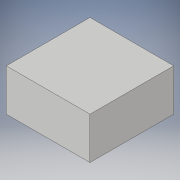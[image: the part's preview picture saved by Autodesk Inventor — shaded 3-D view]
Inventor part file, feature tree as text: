
AUTODESK INVENTOR PART (.ipt)
format: ipt  version: 2018 (Build 220112000, 112)  size: 92,672 bytes
history: native  units: mm
features: extrude x1, shell x1, sketch x1
ambient origin geometry x8: Origin, YZ Plane, XZ Plane, XY Plane, X Axis, Y Axis, Z Axis, Center Point
bodies: Volumenkörper1 (feature_tree)
feature tree (3):
  extrude  "Extrusion1"  Depth=30.0mm
  shell  "Wandung1"  Thickness=15.0mm
  sketch  "Skizze1"  dims[d0=15.0mm d1=30.0mm d2=15.0mm d3=7.5mm d4=30.0mm d5=0.0mm d6=2.0mm]
